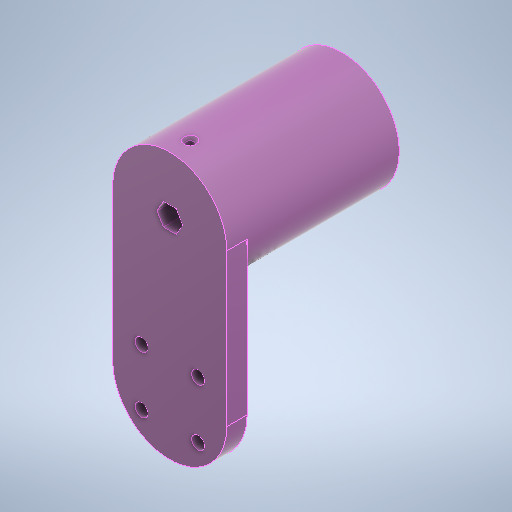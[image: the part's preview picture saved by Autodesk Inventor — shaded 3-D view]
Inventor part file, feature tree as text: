
AUTODESK INVENTOR PART (.ipt)
format: ipt  version: 2025.1 (Build 291241000, 241)  size: 295,424 bytes
history: native  units: mm
features: sketch x4, extrude x2, thicken_offset x1, plane x1, hole x1
ambient origin geometry x8: Origin, YZ Plane, XZ Plane, XY Plane, X Axis, Y Axis, Z Axis, Center Point
bodies: Solid1 (feature_tree)
feature tree (9):
  extrude  "Extrusion1"  Depth=5.0mm
  extrude  "Extrusion2"  Depth=11.14mm
  thicken_offset  "Thicken1"
  plane  "Work Plane1"
  hole  "Hole1"  [1 undecoded]
  sketch  "Sketch1"  dims[d0=45.0mm d3=5.0mm]
  sketch  "Sketch Circular Pattern1"  dims[d4=11.14mm d5=11.14mm]
  sketch  "Sketch2"  dims[d6=40.0mm d8=360.0deg d10=8.0mm d11=0.0mm]
  sketch  "Sketch4"  dims[d12=60.0mm d14=10.0mm d15=60.0mm d16=0.0mm d17=20.0mm d18=20.0mm d19=3.0mm d20=3.0mm d21=3.708mm d22=5.0mm d23=2.0mm d24=14.3117mm d25=18.5mm d26=0.0mm d27=60.0mm d28=60.0mm]
note: 1 required parameter value undecoded (feature->parameter linkage not recoverable at this tier; creation-order binding heuristic only, values carry confidence <= 0.55)
